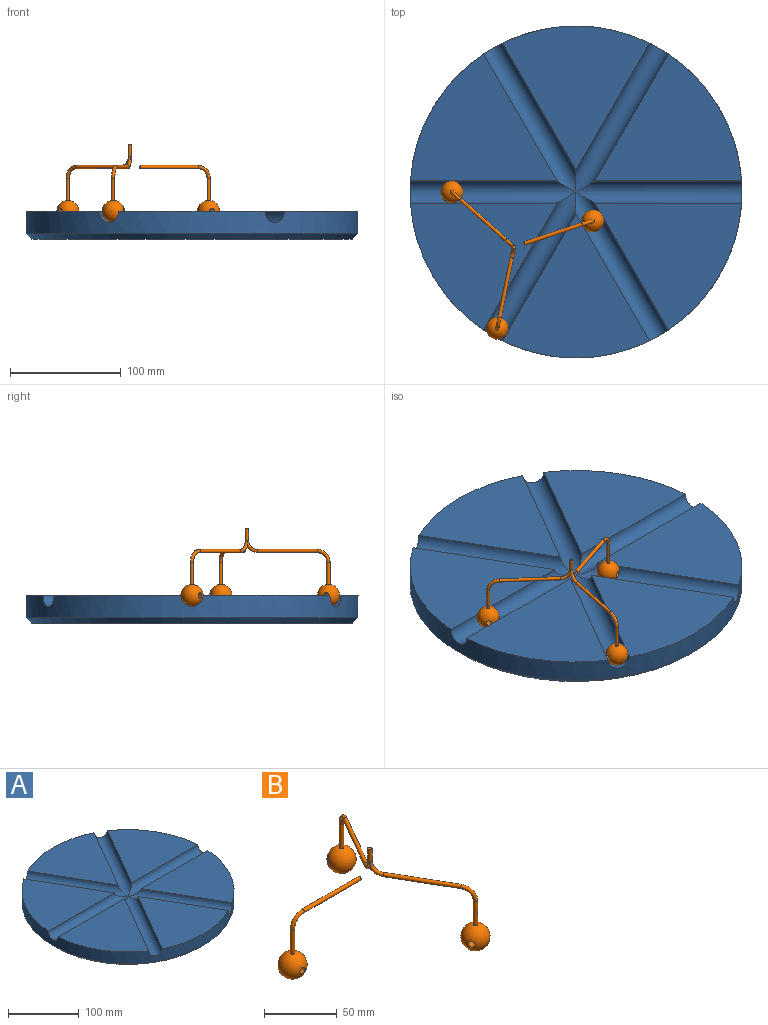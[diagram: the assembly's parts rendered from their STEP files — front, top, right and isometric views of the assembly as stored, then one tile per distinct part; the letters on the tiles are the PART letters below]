
ASSEMBLY  parts=2 mates=1
PART A: 15 faces, bbox 300x300x25 mm
  f0: plane 132.35x114.62mm, normal (0,0,1), area 8956.4mm2, adj f6,f9,f13
  f1: plane 132.35x130mm, normal (0,0,1), area 8956.4mm2, adj f6,f11,f12
  f2: plane 132.35x130mm, normal (0,0,1), area 8956.4mm2, adj f6,f10,f13
  f3: plane 132.35x114.62mm, normal (0,0,1), area 8956.4mm2, adj f6,f9,f11
  f4: cylinder r=10mm len=150mm, axis (1,0,0), area 4360.7mm2, adj f5,f6,f7,f10,f12
  f5: plane 132.35x114.62mm, normal (0,0,1), area 8956.4mm2, adj f4,f6,f10
  f6: cylinder r=150mm len=300mm, axis (0,0,-1), area 17910.4mm2, adj f0,f1,f2,f3,f4,f5,f7,f9
  f7: plane 132.35x114.62mm, normal (0,0,1), area 8956.4mm2, adj f4,f6,f12
  f8: plane 290x290mm, normal (0,0,-1), area 66052mm2, adj f14
  f9: cylinder r=10mm len=150mm, axis (1,0,0), area 4360.7mm2, adj f0,f3,f6,f11,f13
  f10: cylinder r=10mm len=139.9mm, axis (0.5,-0.87,0), area 4360.7mm2, adj f2,f4,f5,f6,f13
  f11: cylinder r=10mm len=139.9mm, axis (0.5,-0.87,0), area 4360.7mm2, adj f1,f3,f6,f9,f12
  f12: cylinder r=10mm len=139.9mm, axis (-0.5,-0.87,0), area 4360.7mm2, adj f1,f4,f6,f7,f11
  f13: cylinder r=10mm len=139.9mm, axis (-0.5,-0.87,0), area 4360.7mm2, adj f0,f2,f6,f9,f10
  f14: cone r=150mm half-angle=45deg, axis (0,0,1), area 6553.3mm2, adj f6,f8
PART B: 21 faces, bbox 132.5x149.9x70 mm
  f0: sphere r=10mm, area 1209.6mm2, adj f1,f2
  f1: cylinder r=2.5mm len=19.37mm, axis (0,1,0), area 304.2mm2, adj f0
  f2: cylinder r=1.5mm len=20.11mm, axis (0,0,-1), area 189.6mm2, adj f0,f3
  f3: torus R=10mm, axis (0,-1,0), area 148mm2, adj f2,f4
  f4: cylinder r=1.5mm len=55mm, axis (-1,0,0), area 518.4mm2, adj f3,f5
  f5: torus R=10mm, axis (0,1,0), area 0mm2, adj f4
  f6: plane 3x3mm, normal (0,0,1), area 7.1mm2, adj f7
  f7: cylinder r=1.5mm len=10mm, axis (0,0,-1), area 94.2mm2, adj f6,f8,f9,f10
  f8: torus R=10mm, axis (-0.87,-0.5,0), area 116.3mm2, adj f7,f9,f10,f11
  f9: torus R=10mm, axis (0.87,-0.5,0), area 116.3mm2, adj f7,f8,f10,f12
  f10: torus R=10mm, axis (0,1,0), area 31.6mm2, adj f7,f8,f9
  f11: cylinder r=1.5mm len=49.13mm, axis (0.5,-0.87,0), area 518.4mm2, adj f8,f13
  f12: cylinder r=1.5mm len=49.13mm, axis (0.5,0.87,0), area 518.4mm2, adj f9,f14
  f13: torus R=10mm, axis (0.87,0.5,0), area 148mm2, adj f11,f15
  f14: torus R=10mm, axis (-0.87,0.5,0), area 148mm2, adj f12,f16
  f15: cylinder r=1.5mm len=20.11mm, axis (0,0,-1), area 189.6mm2, adj f13,f17
  f16: cylinder r=1.5mm len=20.11mm, axis (0,0,-1), area 189.6mm2, adj f14,f18
  f17: sphere r=10mm, area 1209.6mm2, adj f15,f19
  f18: sphere r=10mm, area 1209.6mm2, adj f16,f20
  f19: cylinder r=2.5mm len=19.27mm, axis (-0.87,-0.5,0), area 304.2mm2, adj f17
  f20: cylinder r=2.5mm len=19.27mm, axis (0.87,-0.5,0), area 304.2mm2, adj f18
PLACE A t=(0.54,-0.15,-13.48)mm fixed
PLACE B rot(axis=(0,0,-1),161.6deg) t=(-55.56,-49.93,-38.48)mm
MATE parallel B.f7 <-> A.f6  axis (0,0,1) through (-55.56,-49.93,71.52)mm
